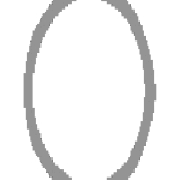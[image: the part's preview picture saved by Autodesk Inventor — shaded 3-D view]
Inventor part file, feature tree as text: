
AUTODESK INVENTOR PART (.ipt)
format: ipt  version: 2021 (Build 250183000, 183)  size: 110,592 bytes
history: native  units: in
note: dims shown in document units (in); Inventor stores cm internally (conversion verified against a paired STEP export)
features: other x4, sketch x3, plane x1
ambient origin geometry x8: Origin, YZ Plane, XZ Plane, XY Plane, X Axis, Y Axis, Z Axis, Center Point
bodies: Solid1 (feature_tree), Body (feature_tree)
feature tree (8):
  other  "Driven Length"
  other  "Frame Generator"
  other  "Start Plane"
  other  "End Plane"
  sketch  "Sketch"  dims[d2=10.9659in d4=-0.0in d5=10.9659in d6=0.12in d7=0.0in d8=90.0deg d9=10.9659in]
  sketch  "Sketch2"  dims[d0=1.0in]
  plane  "Work Plane3"
  sketch  "Sketch3"  dims[d1=0.065in]
